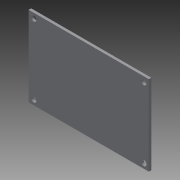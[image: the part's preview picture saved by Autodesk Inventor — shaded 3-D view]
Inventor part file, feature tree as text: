
AUTODESK INVENTOR PART (.ipt)
format: ipt  version: 2013 (Build 170138000, 138)  size: 91,136 bytes
history: native  units: mm
features: extrude x2, sketch x2, other x1
ambient origin geometry x8: Origin, YZ Plane, XZ Plane, XY Plane, X Axis, Y Axis, Z Axis, Center Point
feature tree (5):
  other  "ソリッド1"
  extrude  "押し出し1"  Depth=72.0mm
  extrude  "押し出し2"  Depth=48.0mm
  sketch  "スケッチ1"
  sketch  "スケッチ2"
